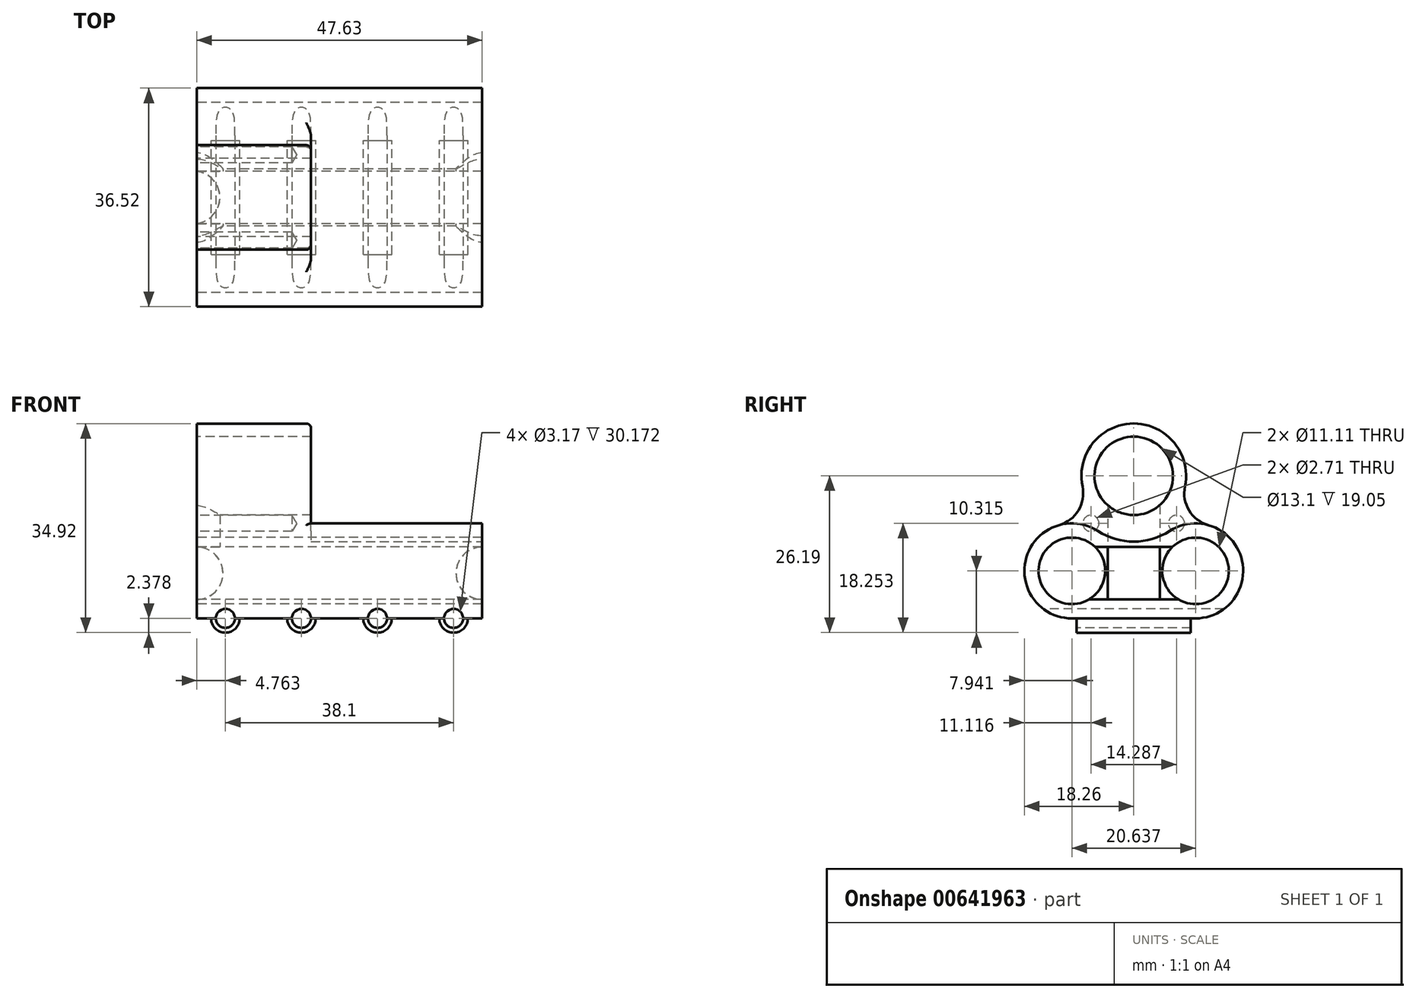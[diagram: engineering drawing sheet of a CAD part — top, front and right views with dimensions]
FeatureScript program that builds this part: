
annotation { "Feature Type Name" : "Feature", "Feature Type Description" : "" }
export const myFeature = defineFeature(function(context is Context, id is Id, definition is map)
    precondition{}
    {
        {
            var Q0;
            Q0=qCreatedBy(makeId("Right.planeOp"),FACE);
            var sketch = newSketch(context, id + "F0", { "sketchPlane" : qUnion([Q0])});
            skCircle(sketch, "E0", {"center": v(0, 0) * mm, "radius": 6.55 * mm});
            skCircle(sketch, "E1", {"center": v(0, 0) * mm, "radius": 8.73 * mm});
            skCircle(sketch, "E2", {"center": v(-10.32, -15.87) * mm, "radius": 5.56 * mm});
            skCircle(sketch, "E3", {"center": v(-10.32, -15.87) * mm, "radius": 7.94 * mm});
            skCircle(sketch, "E4", {"center": v(10.32, -15.87) * mm, "radius": 5.56 * mm});
            skCircle(sketch, "E5", {"center": v(10.32, -15.87) * mm, "radius": 7.94 * mm});
            skArc(sketch, "E6", {"start": v(-12.48, -8.24) * mm, "mid": v(-9.24, -5.77) * mm, "end": v(-8.55, -1.77) * mm});
            skArc(sketch, "E7", {"start": v(8.55, -1.77) * mm, "mid": v(9.24, -5.77) * mm, "end": v(12.48, -8.24) * mm});
            skLineSegment(sketch, "E8", {"start": v(-10.32, -23.81) * mm, "end": v(10.32, -23.81) * mm});
            skSolve(sketch);
        }
        {
            var Q0;
            Q0=makeQuery(id+"F0.imprint","IMPRINT",FACE,{"disambiguationData":[TD([[makeQuery(id+"F0.imprint","IMPRINT",EDGE,{"derivedFrom":sQuery(id+"F0.wireOp",EDGE,"E4")}),-1.0]])]});
            var Q1;
            Q1=makeQuery(id+"F0.imprint","IMPRINT",FACE,{"disambiguationData":[TD([[makeQuery(id+"F0.imprint","IMPRINT",EDGE,{"derivedFrom":sQuery(id+"F0.wireOp",EDGE,"E2")}),-1.0]])]});
            extrude(context, id + "F1", {"entities" : qUnion([Q0, Q1]), "depth" : 47.62 * mm, "offsetDistance" : 25.4 * mm});
        }
        {
            var Q0;
            Q0=makeQuery(id+"F0.imprint","IMPRINT",FACE,{"disambiguationData":[TD([[makeQuery(id+"F0.imprint","IMPRINT",EDGE,{"derivedFrom":sQuery(id+"F0.wireOp",EDGE,"E0")}),-1.0]])]});
            var Q1;
            {var subQ0=sQuery(id+"F0.wireOp",EDGE,"E3");var subQ1=sQuery(id+"F0.wireOp",EDGE,"E1");var subQ2=makeQuery(id+"F0.imprint","INTERSECT",VERTEX,{"disambiguationData":[OD(0.0)],"derivedFrom":[subQ1,subQ0]});Q1=makeQuery(id+"F0.imprint","IMPRINT",FACE,{"disambiguationData":[TD([[makeQuery(id+"F0.imprint","IMPRINT",EDGE,{"disambiguationData":[TD([[subQ2,-1.0]])],"derivedFrom":subQ1}),1.0]])]});}
            var Q2;
            {var subQ0=sQuery(id+"F0.wireOp",EDGE,"E5");var subQ1=sQuery(id+"F0.wireOp",EDGE,"E1");var subQ2=makeQuery(id+"F0.imprint","INTERSECT",VERTEX,{"disambiguationData":[OD(0.0)],"derivedFrom":[subQ1,subQ0]});Q2=makeQuery(id+"F0.imprint","IMPRINT",FACE,{"disambiguationData":[TD([[makeQuery(id+"F0.imprint","IMPRINT",EDGE,{"disambiguationData":[TD([[subQ2,-1.0]])],"derivedFrom":subQ1}),1.0]])]});}
            var Q3;
            {var subQ0=sQuery(id+"F0.wireOp",EDGE,"E6");Q3=makeQuery(id+"F0.imprint","IMPRINT",FACE,{"disambiguationData":[TD([[makeQuery(id+"F0.imprint","IMPRINT",EDGE,{"derivedFrom":subQ0}),-1.0]])]});}
            var Q4;
            {var subQ0=sQuery(id+"F0.wireOp",EDGE,"E7");Q4=makeQuery(id+"F0.imprint","IMPRINT",FACE,{"disambiguationData":[TD([[makeQuery(id+"F0.imprint","IMPRINT",EDGE,{"derivedFrom":subQ0}),-1.0]])]});}
            extrude(context, id + "F2", {"entities" : qUnion([Q0, Q1, Q2, Q3, Q4]), "operationType" : NewBodyOperationType.ADD, "depth" : 19.05 * mm, "offsetDistance" : 25.4 * mm});
        }
        {
            var Q0;
            Q0=makeQuery(id+"F1.opExtrude","CAP_FACE",FACE,{"disambiguationData":[OSD([sQuery(id+"F0.wireOp",EDGE,"E4"),sQuery(id+"F0.wireOp",EDGE,"E5")])],"isStart":false});
            var sketch = newSketch(context, id + "F3", { "sketchPlane" : qUnion([Q0])});
            skArc(sketch, "E9", {"start": v(-6, -9.22) * mm, "mid": v(0, -11) * mm, "end": v(6, -9.22) * mm});
            skCircle(sketch, "E10.0", {"center": v(10.32, -15.87) * mm, "radius": 7.94 * mm});
            skCircle(sketch, "E11.0", {"center": v(-10.32, -15.87) * mm, "radius": 7.94 * mm});
            skLineSegment(sketch, "E12.0", {"start": v(-10.32, -23.81) * mm, "end": v(10.32, -23.81) * mm});
            skSolve(sketch);
        }
        {
            var Q0;
            {var subQ0=sQuery(id+"F3.wireOp",EDGE,"E9");Q0=makeQuery(id+"F3.imprint","IMPRINT",FACE,{"disambiguationData":[TD([[makeQuery(id+"F3.imprint","IMPRINT",EDGE,{"derivedFrom":subQ0}),-1.0]])]});}
            extrude(context, id + "F4", {"entities" : qUnion([Q0]), "operationType" : NewBodyOperationType.ADD, "endBound" : BoundingType.UP_TO_NEXT, "oppositeDirection" : true, "depth" : 25.4 * mm, "offsetDistance" : 25.4 * mm});
        }
        {
            var Q0;
            {var subQ0=sQuery(id+"F0.wireOp",EDGE,"E5");var subQ1=sQuery(id+"F0.wireOp",EDGE,"E3");Q0=makeQuery(id+"F2.boolean.opBoolean","MERGE",FACE,{"derivedFrom":[makeQuery(id+"F1.opExtrude","CAP_FACE",FACE,{"disambiguationData":[OSD([sQuery(id+"F0.wireOp",EDGE,"E2"),subQ1])],"isStart":true}),makeQuery(id+"F1.opExtrude","CAP_FACE",FACE,{"disambiguationData":[OSD([sQuery(id+"F0.wireOp",EDGE,"E4"),subQ0])],"isStart":true}),makeQuery(id+"F2.opExtrude","CAP_FACE",FACE,{"disambiguationData":[OSD([sQuery(id+"F0.wireOp",EDGE,"E0"),sQuery(id+"F0.wireOp",EDGE,"E1"),subQ1,subQ0,sQuery(id+"F0.wireOp",EDGE,"E6"),sQuery(id+"F0.wireOp",EDGE,"E7"),sQuery(id+"F0.wireOp",EDGE,"E8")])],"isStart":true})]});}
            var sketch = newSketch(context, id + "F5", { "sketchPlane" : qUnion([Q0])});
            skLineSegment(sketch, "E13.bottom", {"start": v(4.37, -11.9) * mm, "end": v(-4.37, -11.9) * mm});
            skLineSegment(sketch, "E13.top", {"start": v(4.37, -20.64) * mm, "end": v(-4.37, -20.64) * mm});
            skLineSegment(sketch, "E13.left", {"start": v(4.37, -11.9) * mm, "end": v(4.37, -20.64) * mm});
            skLineSegment(sketch, "E13.right", {"start": v(-4.37, -11.9) * mm, "end": v(-4.37, -20.64) * mm});
            skPoint(sketch, "E13.middle", {"position": v(0, -16.27) * mm});
            skSolve(sketch);
        }
        {
            var Q0;
            {var subQ5=sQuery(id+"F5.wireOp",EDGE,"E13.bottom");Q0=makeQuery(id+"F5.imprint","IMPRINT",FACE,{"disambiguationData":[TD([[makeQuery(id+"F5.imprint","IMPRINT",EDGE,{"derivedFrom":subQ5}),1.0]])]});}
            extrude(context, id + "F6", {"entities" : qUnion([Q0]), "operationType" : NewBodyOperationType.REMOVE, "endBound" : BoundingType.THROUGH_ALL, "oppositeDirection" : true, "depth" : 25.4 * mm, "offsetDistance" : 25.4 * mm});
        }
        {
            var Q0;
            Q0=qCreatedBy(makeId("Front.planeOp"),FACE);
            var sketch = newSketch(context, id + "F7", { "sketchPlane" : qUnion([Q0])});
            skCircle(sketch, "E14", {"center": v(0, -16.27) * mm, "radius": 4.37 * mm});
            skCircle(sketch, "E15", {"center": v(47.63, -16.27) * mm, "radius": 4.37 * mm});
            skSolve(sketch);
        }
        {
            var Q0;
            Q0=makeQuery(id+"F7.imprint","IMPRINT",FACE,{"disambiguationData":[TD([[makeQuery(id+"F7.imprint","IMPRINT",EDGE,{"derivedFrom":sQuery(id+"F7.wireOp",EDGE,"E14")}),1.0]])]});
            var Q1;
            Q1=makeQuery(id+"F7.imprint","IMPRINT",FACE,{"disambiguationData":[TD([[makeQuery(id+"F7.imprint","IMPRINT",EDGE,{"derivedFrom":sQuery(id+"F7.wireOp",EDGE,"E15")}),1.0]])]});
            extrude(context, id + "F8", {"entities" : qUnion([Q0, Q1]), "operationType" : NewBodyOperationType.REMOVE, "oppositeDirection" : true, "depth" : 9.52 * mm, "offsetDistance" : 25.4 * mm, "hasSecondDirection" : true, "secondDirectionOppositeDirection" : false, "secondDirectionDepth" : 9.52 * mm});
        }
        {
            var Q0;
            Q0=makeQuery(id+"F6.boolean.opBoolean","COPY",FACE,{"derivedFrom":makeQuery(id+"F6.opExtrude","SWEPT_FACE",FACE,{"disambiguationData":[OSD([sQuery(id+"F5.wireOp",EDGE,"E13.bottom")])]})});
            var sketch = newSketch(context, id + "F9", { "sketchPlane" : qUnion([Q0])});
            skCircle(sketch, "E16", {"center": v(-0.51, 0) * mm, "radius": 4.37 * mm});
            skSolve(sketch);
        }
        {
            var Q0;
            {var subQ0=sQuery(id+"F9.wireOp",EDGE,"E16");var subQ1=makeQuery(id+"F6.boolean.opBoolean","COPY",EDGE,{"derivedFrom":makeQuery(id+"F6.opExtrude","CAP_EDGE",EDGE,{"disambiguationData":[OSD([sQuery(id+"F5.wireOp",EDGE,"E13.bottom")])],"isStart":true})});var subQ2=makeQuery(id+"F9.imprint","INTERSECT",VERTEX,{"disambiguationData":[OD(0.0)],"derivedFrom":[subQ1,subQ0]});Q0=makeQuery(id+"F9.imprint","IMPRINT",FACE,{"disambiguationData":[TD([[makeQuery(id+"F9.imprint","IMPRINT",EDGE,{"disambiguationData":[TD([[subQ2,1.0]])],"derivedFrom":subQ0}),1.0]])]});}
            var Q1;
            {var subQ0=sQuery(id+"F9.wireOp",EDGE,"E16");var subQ1=makeQuery(id+"F6.boolean.opBoolean","COPY",EDGE,{"derivedFrom":makeQuery(id+"F6.opExtrude","CAP_EDGE",EDGE,{"disambiguationData":[OSD([sQuery(id+"F5.wireOp",EDGE,"E13.bottom")])],"isStart":true})});var subQ2=makeQuery(id+"F9.imprint","INTERSECT",VERTEX,{"disambiguationData":[OD(0.0)],"derivedFrom":[subQ1,subQ0]});Q1=makeQuery(id+"F9.imprint","IMPRINT",FACE,{"disambiguationData":[TD([[makeQuery(id+"F9.imprint","IMPRINT",EDGE,{"disambiguationData":[TD([[subQ2,-1.0]])],"derivedFrom":subQ0}),1.0]])]});}
            extrude(context, id + "F10", {"entities" : qUnion([Q0, Q1]), "operationType" : NewBodyOperationType.REMOVE, "oppositeDirection" : true, "depth" : 9.52 * mm, "offsetDistance" : 25.4 * mm});
        }
        {
            var Q0;
            {var subQ0=sQuery(id+"F0.wireOp",EDGE,"E5");var subQ1=sQuery(id+"F0.wireOp",EDGE,"E3");Q0=makeQuery(id+"F2.boolean.opBoolean","MERGE",FACE,{"derivedFrom":[makeQuery(id+"F1.opExtrude","CAP_FACE",FACE,{"disambiguationData":[OSD([sQuery(id+"F0.wireOp",EDGE,"E2"),subQ1])],"isStart":true}),makeQuery(id+"F1.opExtrude","CAP_FACE",FACE,{"disambiguationData":[OSD([sQuery(id+"F0.wireOp",EDGE,"E4"),subQ0])],"isStart":true}),makeQuery(id+"F2.opExtrude","CAP_FACE",FACE,{"disambiguationData":[OSD([sQuery(id+"F0.wireOp",EDGE,"E0"),sQuery(id+"F0.wireOp",EDGE,"E1"),subQ1,subQ0,sQuery(id+"F0.wireOp",EDGE,"E6"),sQuery(id+"F0.wireOp",EDGE,"E7"),sQuery(id+"F0.wireOp",EDGE,"E8")])],"isStart":true})]});}
            var sketch = newSketch(context, id + "F11", { "sketchPlane" : qUnion([Q0])});
            skPoint(sketch, "E17", {"position": v(7.14, -7.94) * mm});
            skPoint(sketch, "E18", {"position": v(-7.14, -7.94) * mm});
            skSolve(sketch);
        }
        {
            var Q0;
            Q0=sQuery(id+"F11.wireOp",VERTEX,"E17");
            var Q1;
            Q1=sQuery(id+"F11.wireOp",VERTEX,"E18");
            var Q2;
            Q2=makeQuery(id+"F1.opExtrude","SWEPT_BODY",BODY,{"disambiguationData":[OSD([sQuery(id+"F0.wireOp",EDGE,"E2"),sQuery(id+"F0.wireOp",EDGE,"E3")])]});
            hole(context, id + "F12", {"style" : HoleStyle.SIMPLE, "endStyle" : HoleEndStyle.BLIND, "standardTappedOrClearance" : lookupTablePath({ "standard" : "ANSI", "engagement" : "75%", "pitch" : "32 tpi", "size" : "#6", "type" : "Tapped" }), "standardBlindInLast" : lookupTablePath({ "standard" : "ANSI", "engagement" : "75%", "pitch" : "32 tpi", "size" : "#6", "type" : "Tapped" }), "holeDiameter" : 2.7 * mm, "majorDiameter" : 3.5 * mm, "showTappedDepth" : true, "holeDepth" : 15.88 * mm, "isTappedThrough" : true, "tappedDepth" : 13.5 * mm, "tapClearance" : 3, "locations" : qUnion([Q0, Q1]), "scope" : qUnion([Q2])});
        }
        {
            var Q0;
            Q0=makeQuery(id+"F2.opExtrude","CAP_EDGE",EDGE,{"disambiguationData":[OSD([sQuery(id+"F0.wireOp",EDGE,"E1")])],"isStart":false});
            var Q1;
            Q1=makeQuery(id+"F4.opExtrude","CAP_EDGE",EDGE,{"disambiguationData":[OSD([sQuery(id+"F3.wireOp",EDGE,"E9")])],"isStart":false});
            fillet(context, id + "F13", {"entities" : qUnion([Q0, Q1]), "radius" : 0.8 * mm, "tangentPropagation" : true, "allowEdgeOverflow" : false});
        }
        {
            var Q0;
            Q0=qCreatedBy(makeId("Front.planeOp"),FACE);
            var sketch = newSketch(context, id + "F14", { "sketchPlane" : qUnion([Q0])});
            skPoint(sketch, "E19", {"position": v(4.76, -23.81) * mm});
            skPoint(sketch, "E20", {"position": v(17.46, -23.81) * mm});
            skPoint(sketch, "E21", {"position": v(30.16, -23.81) * mm});
            skPoint(sketch, "E22", {"position": v(42.86, -23.81) * mm});
            skCircle(sketch, "E23", {"center": v(4.76, -23.81) * mm, "radius": 2.38 * mm});
            skCircle(sketch, "E24", {"center": v(17.46, -23.81) * mm, "radius": 2.38 * mm});
            skCircle(sketch, "E25", {"center": v(30.16, -23.81) * mm, "radius": 2.38 * mm});
            skCircle(sketch, "E26", {"center": v(42.86, -23.81) * mm, "radius": 2.38 * mm});
            skSolve(sketch);
        }
        {
            var Q0;
            Q0=makeQuery(id+"F14.imprint","IMPRINT",FACE,{"disambiguationData":[TD([[makeQuery(id+"F14.imprint","IMPRINT",EDGE,{"derivedFrom":sQuery(id+"F14.wireOp",EDGE,"E23")}),1.0]])]});
            var Q1;
            Q1=makeQuery(id+"F14.imprint","IMPRINT",FACE,{"disambiguationData":[TD([[makeQuery(id+"F14.imprint","IMPRINT",EDGE,{"derivedFrom":sQuery(id+"F14.wireOp",EDGE,"E24")}),1.0]])]});
            var Q2;
            Q2=makeQuery(id+"F14.imprint","IMPRINT",FACE,{"disambiguationData":[TD([[makeQuery(id+"F14.imprint","IMPRINT",EDGE,{"derivedFrom":sQuery(id+"F14.wireOp",EDGE,"E25")}),1.0]])]});
            var Q3;
            Q3=makeQuery(id+"F14.imprint","IMPRINT",FACE,{"disambiguationData":[TD([[makeQuery(id+"F14.imprint","IMPRINT",EDGE,{"derivedFrom":sQuery(id+"F14.wireOp",EDGE,"E26")}),1.0]])]});
            extrude(context, id + "F15", {"entities" : qUnion([Q0, Q1, Q2, Q3]), "operationType" : NewBodyOperationType.ADD, "depth" : 9.52 * mm, "offsetDistance" : 25.4 * mm, "hasSecondDirection" : true, "secondDirectionOppositeDirection" : true, "secondDirectionDepth" : 9.52 * mm});
        }
        {
            var Q0;
            Q0=makeQuery(id+"F15.opExtrude","CAP_FACE",FACE,{"disambiguationData":[OSD([sQuery(id+"F14.wireOp",EDGE,"E23")])],"isStart":false});
            var sketch = newSketch(context, id + "F16", { "sketchPlane" : qUnion([Q0])});
            skPoint(sketch, "E27", {"position": v(4.76, -23.81) * mm});
            skArc(sketch, "E28.0", {"start": v(15.08, -23.81) * mm, "mid": v(17.46, -26.2) * mm, "end": v(19.84, -23.81) * mm});
            skArc(sketch, "E29.0", {"start": v(40.48, -23.81) * mm, "mid": v(42.86, -26.2) * mm, "end": v(45.24, -23.81) * mm});
            skArc(sketch, "E30.0", {"start": v(27.78, -23.81) * mm, "mid": v(30.16, -26.2) * mm, "end": v(32.54, -23.81) * mm});
            skCircle(sketch, "E31", {"center": v(42.86, -23.81) * mm, "radius": 1.59 * mm});
            skCircle(sketch, "E32", {"center": v(30.16, -23.81) * mm, "radius": 1.59 * mm});
            skCircle(sketch, "E33", {"center": v(17.46, -23.81) * mm, "radius": 1.59 * mm});
            skCircle(sketch, "E34", {"center": v(4.76, -23.81) * mm, "radius": 1.59 * mm});
            skSolve(sketch);
        }
        {
            var Q0;
            Q0=makeQuery(id+"F16.imprint","IMPRINT",FACE,{"disambiguationData":[TD([[makeQuery(id+"F16.imprint","IMPRINT",EDGE,{"derivedFrom":sQuery(id+"F16.wireOp",EDGE,"E31")}),1.0]])]});
            var Q1;
            Q1=makeQuery(id+"F16.imprint","IMPRINT",FACE,{"disambiguationData":[TD([[makeQuery(id+"F16.imprint","IMPRINT",EDGE,{"derivedFrom":sQuery(id+"F16.wireOp",EDGE,"E32")}),1.0]])]});
            var Q2;
            Q2=makeQuery(id+"F16.imprint","IMPRINT",FACE,{"disambiguationData":[TD([[makeQuery(id+"F16.imprint","IMPRINT",EDGE,{"derivedFrom":sQuery(id+"F16.wireOp",EDGE,"E33")}),1.0]])]});
            var Q3;
            {var subQ0=sQuery(id+"F16.wireOp",EDGE,"E34");var subQ1=makeQuery(id+"F15.boolean.opBoolean","INTERSECT",EDGE,{"derivedFrom":[makeQuery(id+"F4.boolean.opBoolean","MERGE",FACE,{"derivedFrom":[makeQuery(id+"F2.opExtrude","SWEPT_FACE",FACE,{"disambiguationData":[OSD([sQuery(id+"F0.wireOp",EDGE,"E8")])]}),makeQuery(id+"F4.opExtrude","SWEPT_FACE",FACE,{"disambiguationData":[OSD([sQuery(id+"F3.wireOp",EDGE,"E12.0")])]})]}),makeQuery(id+"F15.opExtrude","CAP_FACE",FACE,{"disambiguationData":[OSD([sQuery(id+"F14.wireOp",EDGE,"E23")])],"isStart":false})]});var subQ2=makeQuery(id+"F16.imprint","INTERSECT",VERTEX,{"disambiguationData":[OD(0.0)],"derivedFrom":[subQ1,subQ0]});Q3=makeQuery(id+"F16.imprint","IMPRINT",FACE,{"disambiguationData":[TD([[makeQuery(id+"F16.imprint","IMPRINT",EDGE,{"disambiguationData":[TD([[subQ2,-1.0]])],"derivedFrom":subQ0}),1.0]])]});}
            var Q4;
            {var subQ0=sQuery(id+"F16.wireOp",EDGE,"E34");var subQ1=makeQuery(id+"F15.boolean.opBoolean","INTERSECT",EDGE,{"derivedFrom":[makeQuery(id+"F4.boolean.opBoolean","MERGE",FACE,{"derivedFrom":[makeQuery(id+"F2.opExtrude","SWEPT_FACE",FACE,{"disambiguationData":[OSD([sQuery(id+"F0.wireOp",EDGE,"E8")])]}),makeQuery(id+"F4.opExtrude","SWEPT_FACE",FACE,{"disambiguationData":[OSD([sQuery(id+"F3.wireOp",EDGE,"E12.0")])]})]}),makeQuery(id+"F15.opExtrude","CAP_FACE",FACE,{"disambiguationData":[OSD([sQuery(id+"F14.wireOp",EDGE,"E23")])],"isStart":false})]});var subQ2=makeQuery(id+"F16.imprint","INTERSECT",VERTEX,{"disambiguationData":[OD(0.0)],"derivedFrom":[subQ1,subQ0]});Q4=makeQuery(id+"F16.imprint","IMPRINT",FACE,{"disambiguationData":[TD([[makeQuery(id+"F16.imprint","IMPRINT",EDGE,{"disambiguationData":[TD([[subQ2,1.0]])],"derivedFrom":subQ0}),1.0]])]});}
            extrude(context, id + "F17", {"entities" : qUnion([Q0, Q1, Q2, Q3, Q4]), "operationType" : NewBodyOperationType.REMOVE, "endBound" : BoundingType.THROUGH_ALL, "oppositeDirection" : true, "depth" : 25.4 * mm, "offsetDistance" : 25.4 * mm, "hasSecondDirection" : true, "secondDirectionBound" : SecondDirectionBoundingType.THROUGH_ALL, "secondDirectionOppositeDirection" : false, "secondDirectionDepth" : 25.4 * mm});
        }
    });
